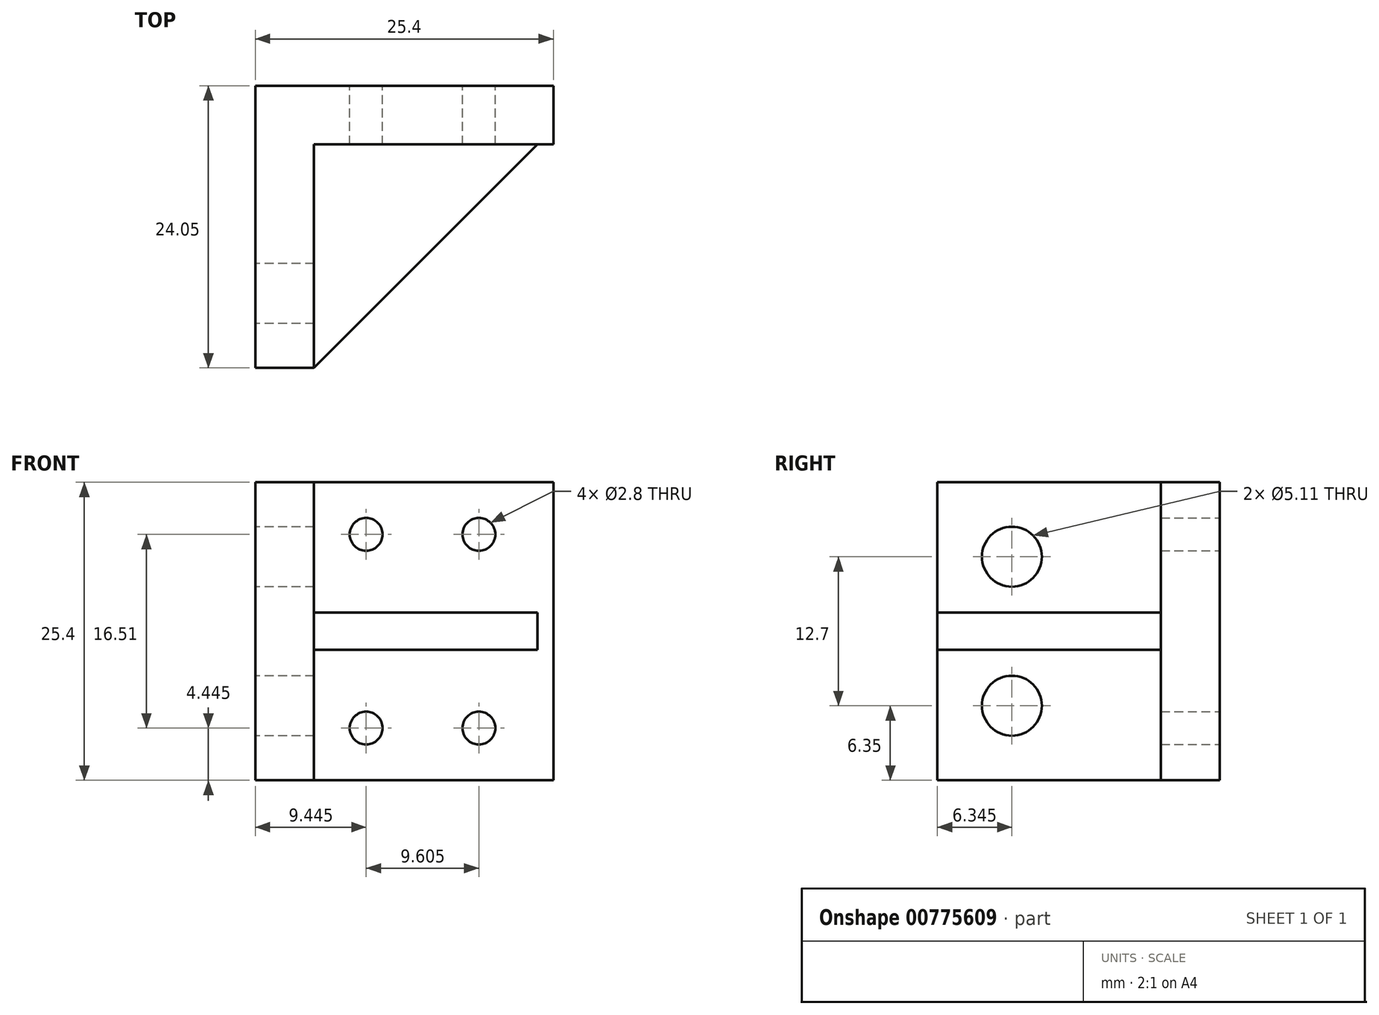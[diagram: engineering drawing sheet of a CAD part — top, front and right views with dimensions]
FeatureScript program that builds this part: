
annotation { "Feature Type Name" : "Feature", "Feature Type Description" : "" }
export const myFeature = defineFeature(function(context is Context, id is Id, definition is map)
    precondition{}
    {
        {
            var Q0;
            Q0=qCreatedBy(makeId("Top.planeOp"),FACE);
            var sketch = newSketch(context, id + "F0", { "sketchPlane" : qUnion([Q0])});
            skLineSegment(sketch, "E0.bottom", {"start": v(-7.7, -12.03) * mm, "end": v(-12.7, -12.03) * mm});
            skLineSegment(sketch, "E0.top", {"start": v(12.7, 12.02) * mm, "end": v(-12.7, 12.02) * mm});
            skLineSegment(sketch, "E0.left", {"start": v(12.7, 7.03) * mm, "end": v(12.7, 12.02) * mm});
            skLineSegment(sketch, "E0.right", {"start": v(-12.7, -12.03) * mm, "end": v(-12.7, 12.02) * mm});
            skPoint(sketch, "E0.middle", {"position": v(0, 0) * mm});
            skLineSegment(sketch, "E1.top", {"start": v(12.7, 7.02) * mm, "end": v(-7.7, 7.02) * mm});
            skLineSegment(sketch, "E1.right", {"start": v(-7.7, -12.03) * mm, "end": v(-7.7, 7.03) * mm});
            skSolve(sketch);
        }
        {
            var Q0;
            Q0 = qSketchRegion(id + "F0", true);
            extrude(context, id + "F1", {"entities" : qUnion([Q0]), "depth" : 25.4 * mm, "offsetDistance" : 25.4 * mm});
        }
        {
            var Q0;
            Q0=makeQuery(id+"F1.opExtrude","SWEPT_FACE",FACE,{"disambiguationData":[OSD([sQuery(id+"F0.wireOp",EDGE,"E1.right")])]});
            var sketch = newSketch(context, id + "F2", { "sketchPlane" : qUnion([Q0])});
            skLineSegment(sketch, "E2.bottom", {"start": v(7.03, 14.29) * mm, "end": v(-12.03, 14.29) * mm});
            skLineSegment(sketch, "E2.top", {"start": v(7.03, 11.11) * mm, "end": v(-12.03, 11.11) * mm});
            skLineSegment(sketch, "E2.left", {"start": v(7.02, 14.29) * mm, "end": v(7.03, 11.11) * mm});
            skLineSegment(sketch, "E2.right", {"start": v(-12.03, 14.29) * mm, "end": v(-12.03, 11.11) * mm});
            skLineSegment(sketch, "E3", {"start": v(7.03, 12.7) * mm, "end": v(-12.03, 12.7) * mm});
            skSolve(sketch);
        }
        {
            var Q0;
            Q0 = qSketchRegion(id + "F2", true);
            extrude(context, id + "F3", {"entities" : qUnion([Q0]), "operationType" : NewBodyOperationType.ADD, "depth" : 25.4 * mm - 5 * mm, "offsetDistance" : 25.4 * mm});
        }
        {
            var Q0;
            Q0=makeQuery(id+"F3.opExtrude","SWEPT_FACE",FACE,{"disambiguationData":[OSD([sQuery(id+"F2.wireOp",EDGE,"E2.bottom")])]});
            var sketch = newSketch(context, id + "F4", { "sketchPlane" : qUnion([Q0])});
            skLineSegment(sketch, "E4", {"start": v(12.7, -12.03) * mm, "end": v(-7.7, -12.03) * mm});
            skLineSegment(sketch, "E5", {"start": v(-7.7, -12.03) * mm, "end": v(11.35, 7.03) * mm});
            skLineSegment(sketch, "E6", {"start": v(11.35, 7.03) * mm, "end": v(12.7, 7.03) * mm});
            skLineSegment(sketch, "E7", {"start": v(12.7, 7.03) * mm, "end": v(12.7, -12.03) * mm});
            skSolve(sketch);
        }
        {
            var Q0;
            Q0 = qSketchRegion(id + "F4", true);
            extrude(context, id + "F5", {"entities" : qUnion([Q0]), "operationType" : NewBodyOperationType.REMOVE, "endBound" : BoundingType.UP_TO_NEXT, "oppositeDirection" : true, "depth" : 25.4 * mm, "offsetDistance" : 25.4 * mm});
        }
        {
            var Q0;
            Q0=makeQuery(id+"F1.opExtrude","SWEPT_FACE",FACE,{"disambiguationData":[OSD([sQuery(id+"F0.wireOp",EDGE,"E0.top")])]});
            var sketch = newSketch(context, id + "F6", { "sketchPlane" : qUnion([Q0])});
            skCircle(sketch, "E8", {"center": v(-6.35, 4.45) * mm, "radius": 1.4 * mm});
            skCircle(sketch, "E9", {"center": v(-6.35, 20.96) * mm, "radius": 1.4 * mm});
            skCircle(sketch, "E10", {"center": v(3.26, 20.96) * mm, "radius": 1.4 * mm});
            skCircle(sketch, "E11", {"center": v(3.26, 4.45) * mm, "radius": 1.4 * mm});
            skSolve(sketch);
        }
        {
            var Q0;
            Q0 = qSketchRegion(id + "F6", true);
            extrude(context, id + "F7", {"entities" : qUnion([Q0]), "operationType" : NewBodyOperationType.REMOVE, "endBound" : BoundingType.UP_TO_NEXT, "oppositeDirection" : true, "depth" : 25.4 * mm, "offsetDistance" : 25.4 * mm});
        }
        {
            var Q0;
            Q0=makeQuery(id+"F1.opExtrude","SWEPT_FACE",FACE,{"disambiguationData":[OSD([sQuery(id+"F0.wireOp",EDGE,"E0.right")])]});
            var sketch = newSketch(context, id + "F8", { "sketchPlane" : qUnion([Q0])});
            skCircle(sketch, "E12", {"center": v(5.68, 19.05) * mm, "radius": 2.55 * mm});
            skCircle(sketch, "E13", {"center": v(5.68, 6.35) * mm, "radius": 2.55 * mm});
            skSolve(sketch);
        }
        {
            var Q0;
            Q0 = qSketchRegion(id + "F8", true);
            extrude(context, id + "F9", {"entities" : qUnion([Q0]), "operationType" : NewBodyOperationType.REMOVE, "endBound" : BoundingType.UP_TO_NEXT, "oppositeDirection" : true, "depth" : 25.4 * mm, "offsetDistance" : 25.4 * mm});
        }
    });
